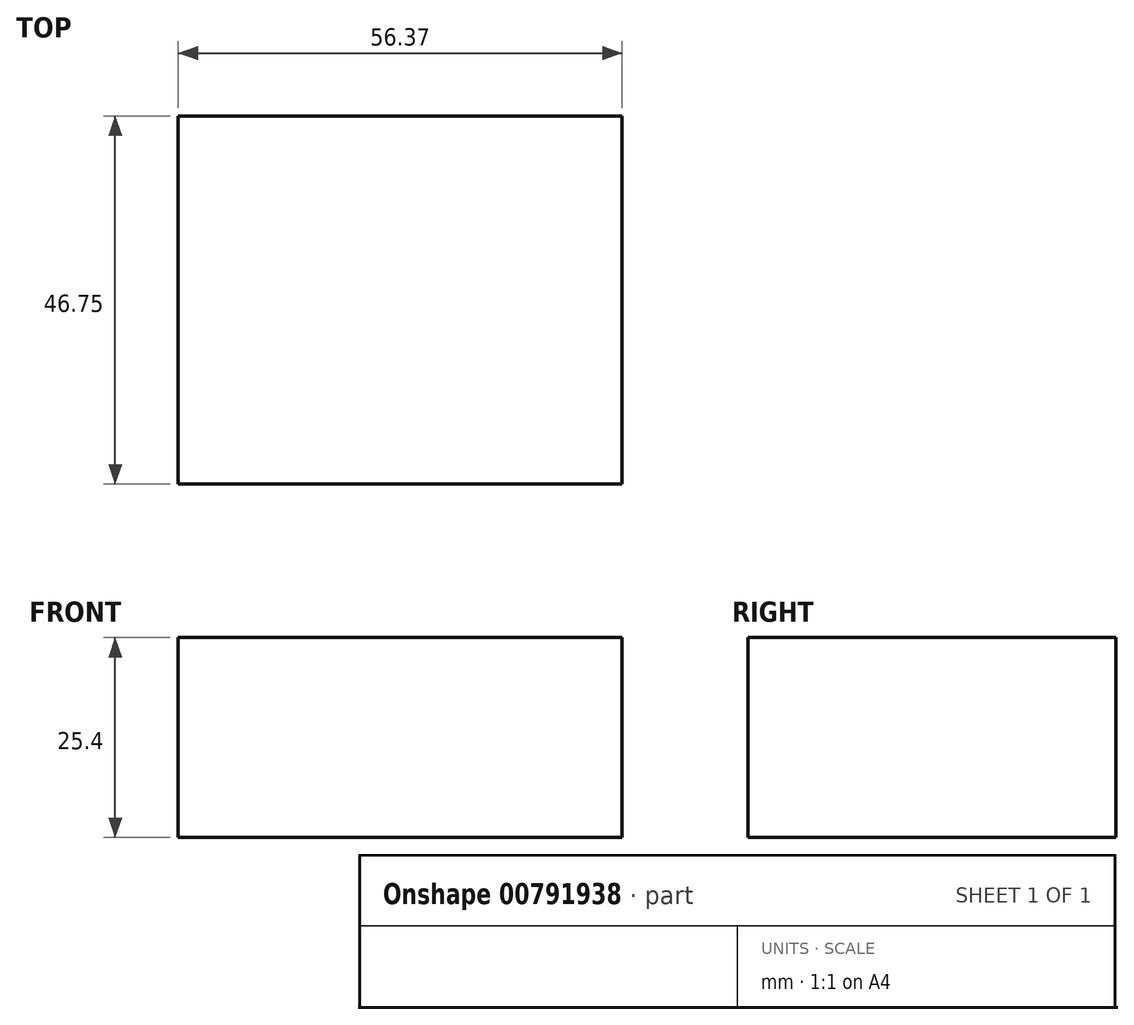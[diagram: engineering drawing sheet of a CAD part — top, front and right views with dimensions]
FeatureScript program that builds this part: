
annotation { "Feature Type Name" : "Feature", "Feature Type Description" : "" }
export const myFeature = defineFeature(function(context is Context, id is Id, definition is map)
    precondition{}
    {
        {
            var Q0;
            Q0=qCreatedBy(makeId("Top.planeOp"),FACE);
            var sketch = newSketch(context, id + "F0", { "sketchPlane" : qUnion([Q0])});
            skLineSegment(sketch, "E0.bottom", {"start": v(0, 0) * mm, "end": v(56.37, 0) * mm});
            skLineSegment(sketch, "E0.top", {"start": v(0, 46.75) * mm, "end": v(56.37, 46.75) * mm});
            skLineSegment(sketch, "E0.left", {"start": v(0, 0) * mm, "end": v(0, 46.75) * mm});
            skLineSegment(sketch, "E0.right", {"start": v(56.37, 0) * mm, "end": v(56.37, 46.75) * mm});
            skLineSegment(sketch, "E1.bottom", {"start": v(30.59, -9.92) * mm, "end": v(39.85, -9.92) * mm});
            skLineSegment(sketch, "E1.top", {"start": v(30.59, -23.8) * mm, "end": v(39.85, -23.8) * mm});
            skLineSegment(sketch, "E1.left", {"start": v(30.59, -9.92) * mm, "end": v(30.59, -23.8) * mm});
            skLineSegment(sketch, "E1.right", {"start": v(39.85, -9.92) * mm, "end": v(39.85, -23.8) * mm});
            skSolve(sketch);
        }
        {
            var Q0;
            Q0=makeQuery(id+"F0.imprint","IMPRINT",FACE,{"disambiguationData":[TD([[makeQuery(id+"F0.imprint","IMPRINT",EDGE,{"derivedFrom":sQuery(id+"F0.wireOp",EDGE,"E0.bottom")}),1.0]])]});
            extrude(context, id + "F1", {"entities" : qUnion([Q0]), "depth" : 25.4 * mm, "offsetDistance" : 25.4 * mm});
        }
    });
